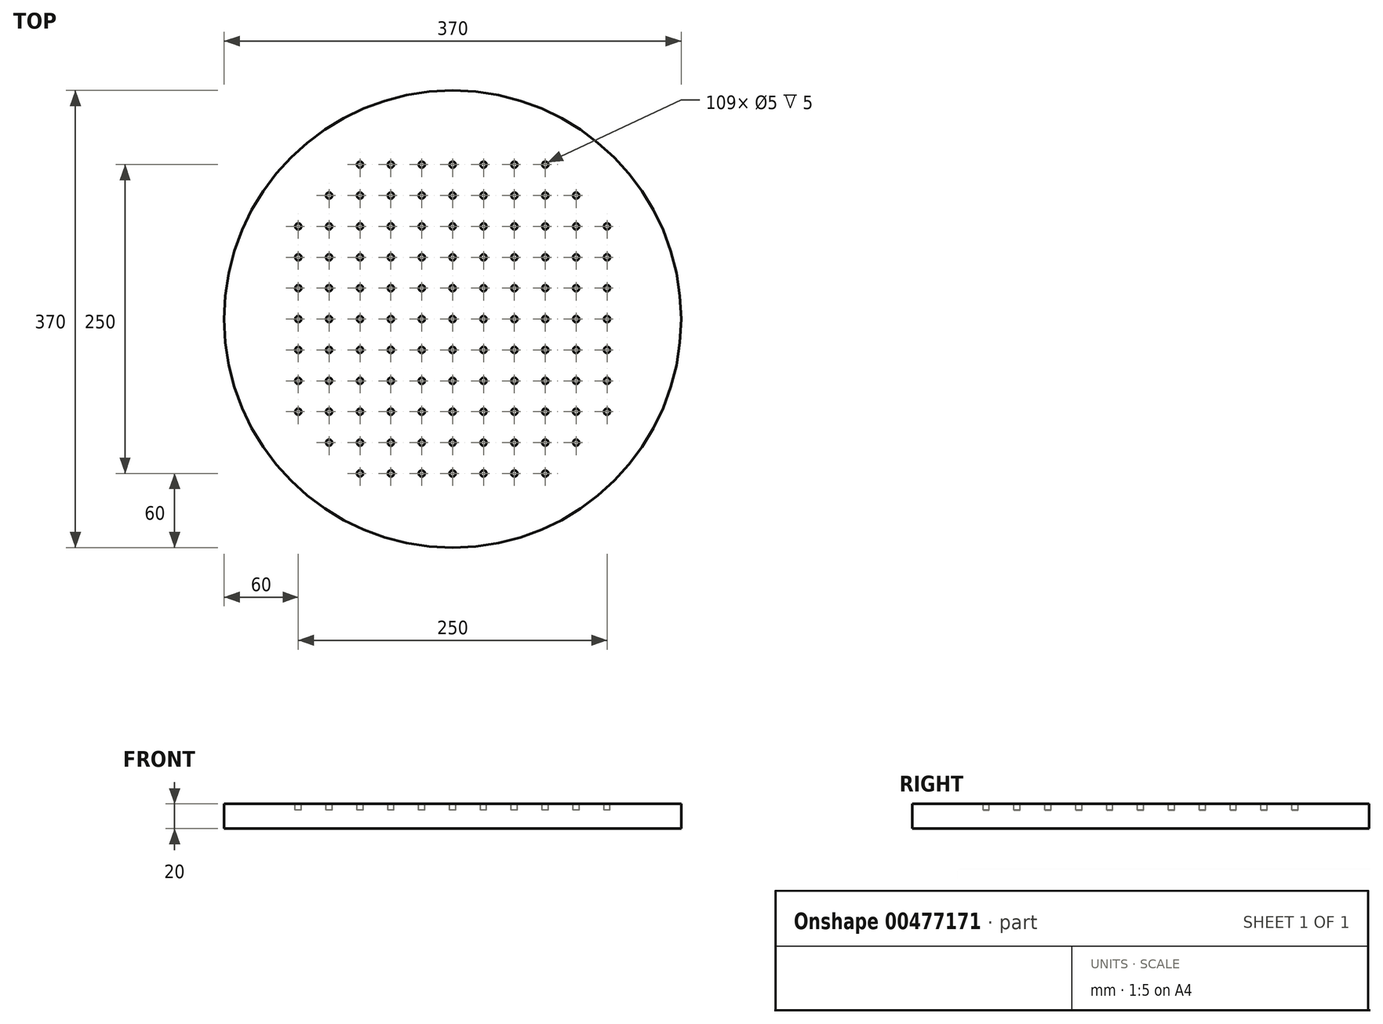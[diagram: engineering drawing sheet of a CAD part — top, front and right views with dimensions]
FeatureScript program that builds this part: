
annotation { "Feature Type Name" : "Feature", "Feature Type Description" : "" }
export const myFeature = defineFeature(function(context is Context, id is Id, definition is map)
    precondition{}
    {
        {
            var Q0;
            Q0=qCreatedBy(makeId("Top.planeOp"),FACE);
            var sketch = newSketch(context, id + "F0", { "sketchPlane" : qUnion([Q0])});
            skCircle(sketch, "E0", {"center": v(0, 0) * mm, "radius": 185 * mm});
            skSolve(sketch);
        }
        {
            var Q0;
            Q0=makeQuery(id+"F0.imprint","IMPRINT",FACE,{"disambiguationData":[TD([[makeQuery(id+"F0.imprint","IMPRINT",EDGE,{"derivedFrom":sQuery(id+"F0.wireOp",EDGE,"E0")}),1.0]])]});
            extrude(context, id + "F1", {"entities" : qUnion([Q0]), "depth" : 20 * mm});
        }
        {
            var Q0;
            Q0=makeQuery(id+"F1.opExtrude","CAP_FACE",FACE,{"disambiguationData":[OSD([sQuery(id+"F0.wireOp",EDGE,"E0")])],"isStart":false});
            var sketch = newSketch(context, id + "F2", { "sketchPlane" : qUnion([Q0])});
            skCircle(sketch, "E1", {"center": v(0, 0) * mm, "radius": 160 * mm});
            skCircle(sketch, "E2.0", {"center": v(0, 0) * mm, "radius": 157 * mm});
            skSolve(sketch);
        }
        {
            var Q0;
            Q0=sQuery(id+"F2.wireOp",EDGE,"E1");
            var Q1;
            Q1=sQuery(id+"F2.wireOp",EDGE,"E2.0");
            extrude(context, id + "F3", {"bodyType" : ToolBodyType.SURFACE, "surfaceEntities" : qUnion([Q0, Q1]), "oppositeDirection" : true, "depth" : 5 * mm});
        }
        {
            var Q0;
            Q0=makeQuery(id+"F1.opExtrude","CAP_FACE",FACE,{"disambiguationData":[OSD([sQuery(id+"F0.wireOp",EDGE,"E0")])],"isStart":false});
            var sketch = newSketch(context, id + "F4", { "sketchPlane" : qUnion([Q0])});
            skCircle(sketch, "E3", {"center": v(0, 0) * mm, "radius": 2.5 * mm});
            skCircle(sketch, "E4.0.1.0", {"center": v(0, 25) * mm, "radius": 2.5 * mm});
            skCircle(sketch, "E4.0.2.0", {"center": v(0, 50) * mm, "radius": 2.5 * mm});
            skCircle(sketch, "E4.0.3.0", {"center": v(0, 75) * mm, "radius": 2.5 * mm});
            skCircle(sketch, "E4.0.4.0", {"center": v(0, 100) * mm, "radius": 2.5 * mm});
            skCircle(sketch, "E4.0.5.0", {"center": v(0, 125) * mm, "radius": 2.5 * mm});
            skCircle(sketch, "E4.1.0.0", {"center": v(25, 0) * mm, "radius": 2.5 * mm});
            skCircle(sketch, "E4.1.1.0", {"center": v(25, 25) * mm, "radius": 2.5 * mm});
            skCircle(sketch, "E4.1.2.0", {"center": v(25, 50) * mm, "radius": 2.5 * mm});
            skCircle(sketch, "E4.1.3.0", {"center": v(25, 75) * mm, "radius": 2.5 * mm});
            skCircle(sketch, "E4.1.4.0", {"center": v(25, 100) * mm, "radius": 2.5 * mm});
            skCircle(sketch, "E4.1.5.0", {"center": v(25, 125) * mm, "radius": 2.5 * mm});
            skCircle(sketch, "E4.2.0.0", {"center": v(50, 0) * mm, "radius": 2.5 * mm});
            skCircle(sketch, "E4.2.1.0", {"center": v(50, 25) * mm, "radius": 2.5 * mm});
            skCircle(sketch, "E4.2.2.0", {"center": v(50, 50) * mm, "radius": 2.5 * mm});
            skCircle(sketch, "E4.2.3.0", {"center": v(50, 75) * mm, "radius": 2.5 * mm});
            skCircle(sketch, "E4.2.4.0", {"center": v(50, 100) * mm, "radius": 2.5 * mm});
            skCircle(sketch, "E4.2.5.0", {"center": v(50, 125) * mm, "radius": 2.5 * mm});
            skCircle(sketch, "E4.3.0.0", {"center": v(75, 0) * mm, "radius": 2.5 * mm});
            skCircle(sketch, "E4.3.1.0", {"center": v(75, 25) * mm, "radius": 2.5 * mm});
            skCircle(sketch, "E4.3.2.0", {"center": v(75, 50) * mm, "radius": 2.5 * mm});
            skCircle(sketch, "E4.3.3.0", {"center": v(75, 75) * mm, "radius": 2.5 * mm});
            skCircle(sketch, "E4.3.4.0", {"center": v(75, 100) * mm, "radius": 2.5 * mm});
            skCircle(sketch, "E4.3.5.0", {"center": v(75, 125) * mm, "radius": 2.5 * mm});
            skCircle(sketch, "E4.4.0.0", {"center": v(100, 0) * mm, "radius": 2.5 * mm});
            skCircle(sketch, "E4.4.1.0", {"center": v(100, 25) * mm, "radius": 2.5 * mm});
            skCircle(sketch, "E4.4.2.0", {"center": v(100, 50) * mm, "radius": 2.5 * mm});
            skCircle(sketch, "E4.4.3.0", {"center": v(100, 75) * mm, "radius": 2.5 * mm});
            skCircle(sketch, "E4.4.4.0", {"center": v(100, 100) * mm, "radius": 2.5 * mm});
            skCircle(sketch, "E4.5.0.0", {"center": v(125, 0) * mm, "radius": 2.5 * mm});
            skCircle(sketch, "E4.5.1.0", {"center": v(125, 25) * mm, "radius": 2.5 * mm});
            skCircle(sketch, "E4.5.2.0", {"center": v(125, 50) * mm, "radius": 2.5 * mm});
            skCircle(sketch, "E4.5.3.0", {"center": v(125, 75) * mm, "radius": 2.5 * mm});
            skLineSegment(sketch, "E4.direction1", {"start": v(0, 0) * mm, "end": v(25, 0) * mm, "construction": true});
            skLineSegment(sketch, "E4.direction2", {"start": v(0, 0) * mm, "end": v(0, 25) * mm, "construction": true});
            skLineSegment(sketch, "E5.1.0", {"start": v(0, 0) * mm, "end": v(0, -25) * mm, "construction": true});
            skCircle(sketch, "E5.1.2", {"center": v(75, -25) * mm, "radius": 2.5 * mm});
            skCircle(sketch, "E5.1.3", {"center": v(100, -50) * mm, "radius": 2.5 * mm});
            skCircle(sketch, "E5.1.4", {"center": v(0, -100) * mm, "radius": 2.5 * mm});
            skCircle(sketch, "E5.1.5", {"center": v(100, -100) * mm, "radius": 2.5 * mm});
            skCircle(sketch, "E5.1.6", {"center": v(75, -100) * mm, "radius": 2.5 * mm});
            skCircle(sketch, "E5.1.7", {"center": v(125, -50) * mm, "radius": 2.5 * mm});
            skCircle(sketch, "E5.1.8", {"center": v(75, -125) * mm, "radius": 2.5 * mm});
            skCircle(sketch, "E5.1.10", {"center": v(25, -50) * mm, "radius": 2.5 * mm});
            skCircle(sketch, "E5.1.12", {"center": v(0, -75) * mm, "radius": 2.5 * mm});
            skCircle(sketch, "E5.1.14", {"center": v(100, -75) * mm, "radius": 2.5 * mm});
            skCircle(sketch, "E5.1.16", {"center": v(100, -25) * mm, "radius": 2.5 * mm});
            skCircle(sketch, "E5.1.17", {"center": v(50, -125) * mm, "radius": 2.5 * mm});
            skCircle(sketch, "E5.1.18", {"center": v(125, -25) * mm, "radius": 2.5 * mm});
            skCircle(sketch, "E5.1.19", {"center": v(50, -75) * mm, "radius": 2.5 * mm});
            skCircle(sketch, "E5.1.20", {"center": v(25, -25) * mm, "radius": 2.5 * mm});
            skCircle(sketch, "E5.1.21", {"center": v(75, -75) * mm, "radius": 2.5 * mm});
            skCircle(sketch, "E5.1.22", {"center": v(75, -50) * mm, "radius": 2.5 * mm});
            skCircle(sketch, "E5.1.23", {"center": v(125, -75) * mm, "radius": 2.5 * mm});
            skCircle(sketch, "E5.1.24", {"center": v(0, -125) * mm, "radius": 2.5 * mm});
            skCircle(sketch, "E5.1.25", {"center": v(25, -75) * mm, "radius": 2.5 * mm});
            skCircle(sketch, "E5.1.26", {"center": v(50, -100) * mm, "radius": 2.5 * mm});
            skCircle(sketch, "E5.1.27", {"center": v(25, -125) * mm, "radius": 2.5 * mm});
            skCircle(sketch, "E5.1.28", {"center": v(0, -50) * mm, "radius": 2.5 * mm});
            skCircle(sketch, "E5.1.29", {"center": v(25, -100) * mm, "radius": 2.5 * mm});
            skCircle(sketch, "E5.1.30", {"center": v(50, -25) * mm, "radius": 2.5 * mm});
            skCircle(sketch, "E5.1.31", {"center": v(50, -50) * mm, "radius": 2.5 * mm});
            skCircle(sketch, "E5.1.32", {"center": v(0, -25) * mm, "radius": 2.5 * mm});
            skLineSegment(sketch, "E5.2.0", {"start": v(0, 0) * mm, "end": v(-25, 0) * mm, "construction": true});
            skLineSegment(sketch, "E5.2.1", {"start": v(0, 0) * mm, "end": v(0, -25) * mm, "construction": true});
            skCircle(sketch, "E5.2.2", {"center": v(-25, -75) * mm, "radius": 2.5 * mm});
            skCircle(sketch, "E5.2.3", {"center": v(-50, -100) * mm, "radius": 2.5 * mm});
            skCircle(sketch, "E5.2.4", {"center": v(-100, 0) * mm, "radius": 2.5 * mm});
            skCircle(sketch, "E5.2.5", {"center": v(-100, -100) * mm, "radius": 2.5 * mm});
            skCircle(sketch, "E5.2.6", {"center": v(-100, -75) * mm, "radius": 2.5 * mm});
            skCircle(sketch, "E5.2.7", {"center": v(-50, -125) * mm, "radius": 2.5 * mm});
            skCircle(sketch, "E5.2.8", {"center": v(-125, -75) * mm, "radius": 2.5 * mm});
            skCircle(sketch, "E5.2.9", {"center": v(0, -75) * mm, "radius": 2.5 * mm});
            skCircle(sketch, "E5.2.10", {"center": v(-50, -25) * mm, "radius": 2.5 * mm});
            skCircle(sketch, "E5.2.11", {"center": v(0, -100) * mm, "radius": 2.5 * mm});
            skCircle(sketch, "E5.2.12", {"center": v(-75, 0) * mm, "radius": 2.5 * mm});
            skCircle(sketch, "E5.2.13", {"center": v(0, -125) * mm, "radius": 2.5 * mm});
            skCircle(sketch, "E5.2.14", {"center": v(-75, -100) * mm, "radius": 2.5 * mm});
            skCircle(sketch, "E5.2.15", {"center": v(0, -50) * mm, "radius": 2.5 * mm});
            skCircle(sketch, "E5.2.16", {"center": v(-25, -100) * mm, "radius": 2.5 * mm});
            skCircle(sketch, "E5.2.17", {"center": v(-125, -50) * mm, "radius": 2.5 * mm});
            skCircle(sketch, "E5.2.18", {"center": v(-25, -125) * mm, "radius": 2.5 * mm});
            skCircle(sketch, "E5.2.19", {"center": v(-75, -50) * mm, "radius": 2.5 * mm});
            skCircle(sketch, "E5.2.20", {"center": v(-25, -25) * mm, "radius": 2.5 * mm});
            skCircle(sketch, "E5.2.21", {"center": v(-75, -75) * mm, "radius": 2.5 * mm});
            skCircle(sketch, "E5.2.22", {"center": v(-50, -75) * mm, "radius": 2.5 * mm});
            skCircle(sketch, "E5.2.23", {"center": v(-75, -125) * mm, "radius": 2.5 * mm});
            skCircle(sketch, "E5.2.24", {"center": v(-125, 0) * mm, "radius": 2.5 * mm});
            skCircle(sketch, "E5.2.25", {"center": v(-75, -25) * mm, "radius": 2.5 * mm});
            skCircle(sketch, "E5.2.26", {"center": v(-100, -50) * mm, "radius": 2.5 * mm});
            skCircle(sketch, "E5.2.27", {"center": v(-125, -25) * mm, "radius": 2.5 * mm});
            skCircle(sketch, "E5.2.28", {"center": v(-50, 0) * mm, "radius": 2.5 * mm});
            skCircle(sketch, "E5.2.29", {"center": v(-100, -25) * mm, "radius": 2.5 * mm});
            skCircle(sketch, "E5.2.30", {"center": v(-25, -50) * mm, "radius": 2.5 * mm});
            skCircle(sketch, "E5.2.31", {"center": v(-50, -50) * mm, "radius": 2.5 * mm});
            skCircle(sketch, "E5.2.32", {"center": v(-25, 0) * mm, "radius": 2.5 * mm});
            skCircle(sketch, "E5.2.33", {"center": v(0, -25) * mm, "radius": 2.5 * mm});
            skLineSegment(sketch, "E5.3.1", {"start": v(0, 0) * mm, "end": v(-25, 0) * mm, "construction": true});
            skCircle(sketch, "E5.3.2", {"center": v(-75, 25) * mm, "radius": 2.5 * mm});
            skCircle(sketch, "E5.3.3", {"center": v(-100, 50) * mm, "radius": 2.5 * mm});
            skCircle(sketch, "E5.3.5", {"center": v(-100, 100) * mm, "radius": 2.5 * mm});
            skCircle(sketch, "E5.3.6", {"center": v(-75, 100) * mm, "radius": 2.5 * mm});
            skCircle(sketch, "E5.3.7", {"center": v(-125, 50) * mm, "radius": 2.5 * mm});
            skCircle(sketch, "E5.3.8", {"center": v(-75, 125) * mm, "radius": 2.5 * mm});
            skCircle(sketch, "E5.3.9", {"center": v(-75, 0) * mm, "radius": 2.5 * mm});
            skCircle(sketch, "E5.3.10", {"center": v(-25, 50) * mm, "radius": 2.5 * mm});
            skCircle(sketch, "E5.3.11", {"center": v(-100, 0) * mm, "radius": 2.5 * mm});
            skCircle(sketch, "E5.3.13", {"center": v(-125, 0) * mm, "radius": 2.5 * mm});
            skCircle(sketch, "E5.3.14", {"center": v(-100, 75) * mm, "radius": 2.5 * mm});
            skCircle(sketch, "E5.3.15", {"center": v(-50, 0) * mm, "radius": 2.5 * mm});
            skCircle(sketch, "E5.3.16", {"center": v(-100, 25) * mm, "radius": 2.5 * mm});
            skCircle(sketch, "E5.3.17", {"center": v(-50, 125) * mm, "radius": 2.5 * mm});
            skCircle(sketch, "E5.3.18", {"center": v(-125, 25) * mm, "radius": 2.5 * mm});
            skCircle(sketch, "E5.3.19", {"center": v(-50, 75) * mm, "radius": 2.5 * mm});
            skCircle(sketch, "E5.3.20", {"center": v(-25, 25) * mm, "radius": 2.5 * mm});
            skCircle(sketch, "E5.3.21", {"center": v(-75, 75) * mm, "radius": 2.5 * mm});
            skCircle(sketch, "E5.3.22", {"center": v(-75, 50) * mm, "radius": 2.5 * mm});
            skCircle(sketch, "E5.3.23", {"center": v(-125, 75) * mm, "radius": 2.5 * mm});
            skCircle(sketch, "E5.3.25", {"center": v(-25, 75) * mm, "radius": 2.5 * mm});
            skCircle(sketch, "E5.3.26", {"center": v(-50, 100) * mm, "radius": 2.5 * mm});
            skCircle(sketch, "E5.3.27", {"center": v(-25, 125) * mm, "radius": 2.5 * mm});
            skCircle(sketch, "E5.3.29", {"center": v(-25, 100) * mm, "radius": 2.5 * mm});
            skCircle(sketch, "E5.3.30", {"center": v(-50, 25) * mm, "radius": 2.5 * mm});
            skCircle(sketch, "E5.3.31", {"center": v(-50, 50) * mm, "radius": 2.5 * mm});
            skCircle(sketch, "E5.3.33", {"center": v(-25, 0) * mm, "radius": 2.5 * mm});
            skSolve(sketch);
        }
        {
            var Q0;
            Q0 = qSketchRegion(id + "F4", true);
            extrude(context, id + "F5", {"entities" : qUnion([Q0]), "operationType" : NewBodyOperationType.REMOVE, "oppositeDirection" : true, "depth" : 5 * mm});
        }
    });
